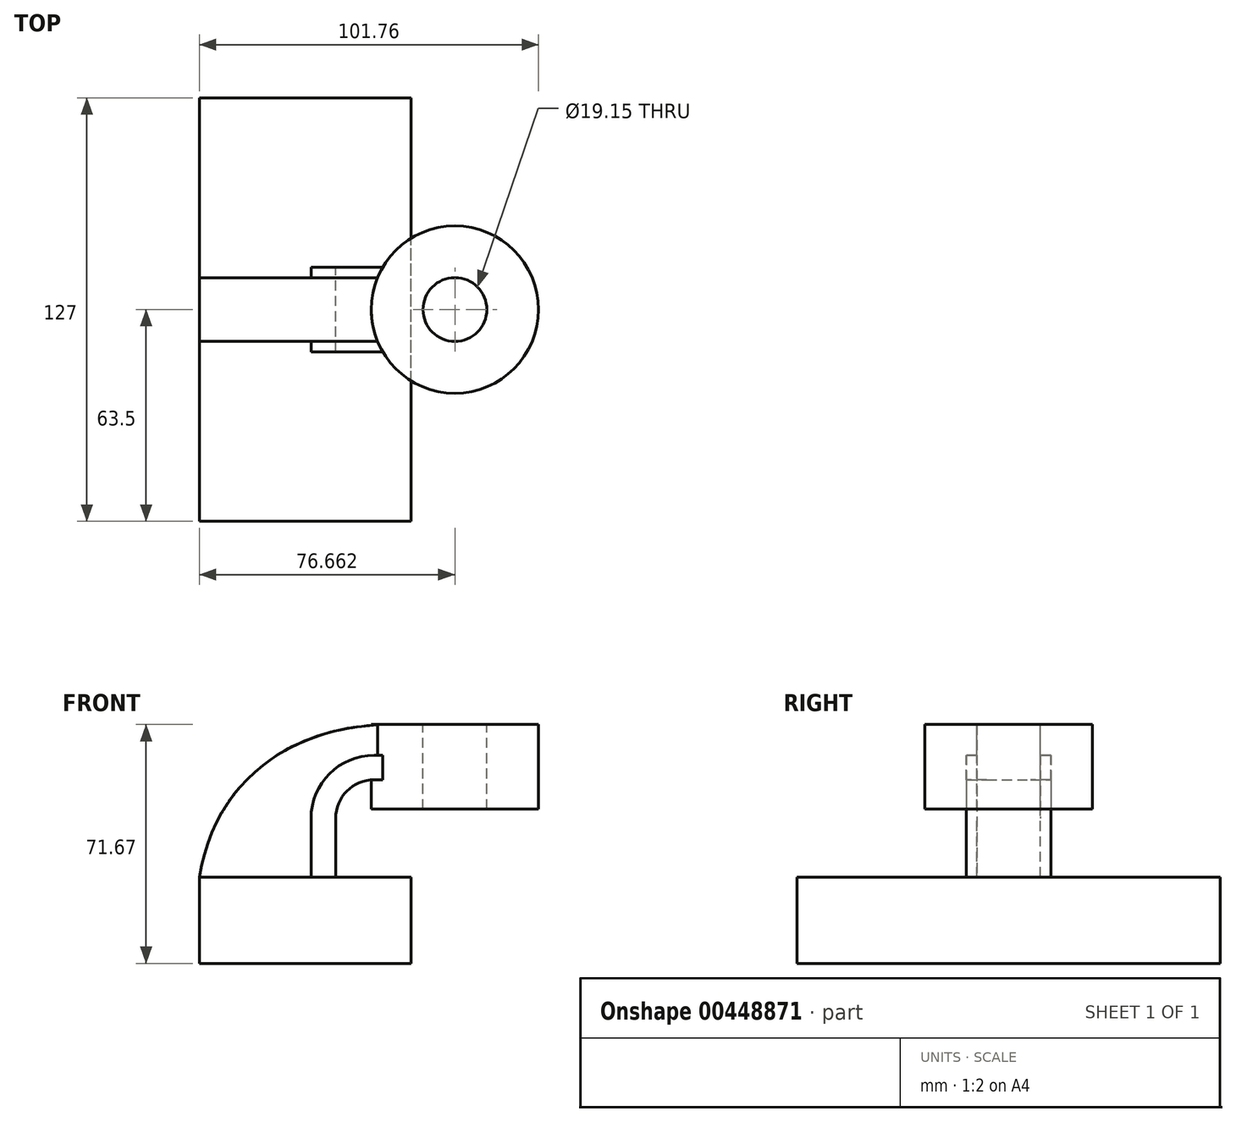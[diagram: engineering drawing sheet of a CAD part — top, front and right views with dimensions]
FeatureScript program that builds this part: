
annotation { "Feature Type Name" : "Feature", "Feature Type Description" : "" }
export const myFeature = defineFeature(function(context is Context, id is Id, definition is map)
    precondition{}
    {
        {
            var Q0;
            Q0=qCreatedBy(makeId("Front.planeOp"),FACE);
            var sketch = newSketch(context, id + "F0", { "sketchPlane" : qUnion([Q0])});
            skLineSegment(sketch, "E0.bottom", {"start": v(31.75, -12.95) * mm, "end": v(-31.75, -12.95) * mm});
            skLineSegment(sketch, "E0.top", {"start": v(31.75, 12.95) * mm, "end": v(-31.75, 12.95) * mm});
            skLineSegment(sketch, "E0.left", {"start": v(31.75, -12.95) * mm, "end": v(31.75, 12.95) * mm});
            skLineSegment(sketch, "E0.right", {"start": v(-31.75, -12.95) * mm, "end": v(-31.75, 12.95) * mm});
            skPoint(sketch, "E0.middle", {"position": v(0, 0) * mm});
            skLineSegment(sketch, "E1.bottom", {"start": v(64.65, 35.11) * mm, "end": v(25.17, 35.11) * mm});
            skLineSegment(sketch, "E1.top", {"start": v(64.65, 58.72) * mm, "end": v(25.17, 58.72) * mm});
            skLineSegment(sketch, "E1.left", {"start": v(64.65, 35.11) * mm, "end": v(64.65, 58.72) * mm});
            skLineSegment(sketch, "E1.right", {"start": v(25.17, 35.11) * mm, "end": v(25.17, 58.72) * mm});
            skPoint(sketch, "E1.middle", {"position": v(44.91, 46.92) * mm});
            skLineSegment(sketch, "E2", {"start": v(9.11, 12.95) * mm, "end": v(9.11, 30.56) * mm});
            skArc(sketch, "E3", {"start": v(9.11, 30.56) * mm, "mid": v(12.5, 38.74) * mm, "end": v(20.69, 42.14) * mm});
            skLineSegment(sketch, "E4", {"start": v(20.69, 42.14) * mm, "end": v(60.17, 42.14) * mm});
            skFitSpline(sketch, "E5", {"points": [v(-31.75, 12.95) * mm, v(25.17, 58.72) * mm], "startDerivative": vector(14.1, 86.06) * mm, "endDerivative": vector(90.2, 1.27) * mm});
            skLineSegment(sketch, "E6.0", {"start": v(20.69, 49.5) * mm, "end": v(60.17, 49.5) * mm});
            skArc(sketch, "E6.1", {"start": v(1.74, 30.56) * mm, "mid": v(7.3, 43.95) * mm, "end": v(20.69, 49.5) * mm});
            skLineSegment(sketch, "E6.2", {"start": v(1.74, 12.95) * mm, "end": v(1.74, 30.56) * mm});
            skLineSegment(sketch, "E7", {"start": v(44.91, 58.72) * mm, "end": v(44.91, 35.11) * mm});
            skSolve(sketch);
        }
        {
            var Q0;
            Q0=makeQuery(id+"F0.imprint","IMPRINT",FACE,{"disambiguationData":[TD([[makeQuery(id+"F0.imprint","IMPRINT",EDGE,{"derivedFrom":sQuery(id+"F0.wireOp",EDGE,"E0.bottom")}),-1.0]])]});
            extrude(context, id + "F1", {"entities" : qUnion([Q0]), "endBound" : BoundingType.SYMMETRIC, "depth" : 127 * mm});
        }
        {
            var Q0;
            {var subQ0=sQuery(id+"F0.wireOp",EDGE,"E5");Q0=makeQuery(id+"F0.imprint","IMPRINT",FACE,{"disambiguationData":[TD([[makeQuery(id+"F0.imprint","IMPRINT",EDGE,{"derivedFrom":subQ0}),-1.0]])]});}
            extrude(context, id + "F2", {"entities" : qUnion([Q0]), "operationType" : NewBodyOperationType.ADD, "endBound" : BoundingType.SYMMETRIC, "depth" : 19.05 * mm});
        }
        {
            var Q0;
            {var subQ1=sQuery(id+"F0.wireOp",EDGE,"E2");Q0=makeQuery(id+"F0.imprint","IMPRINT",FACE,{"disambiguationData":[TD([[makeQuery(id+"F0.imprint","IMPRINT",EDGE,{"derivedFrom":subQ1}),1.0]])]});}
            extrude(context, id + "F3", {"entities" : qUnion([Q0]), "operationType" : NewBodyOperationType.ADD, "endBound" : BoundingType.SYMMETRIC, "depth" : 25.4 * mm});
        }
        {
            var Q0;
            {var subQ0=sQuery(id+"F0.wireOp",EDGE,"E1.left");Q0=makeQuery(id+"F0.imprint","IMPRINT",FACE,{"disambiguationData":[TD([[makeQuery(id+"F0.imprint","IMPRINT",EDGE,{"derivedFrom":subQ0}),1.0]])]});}
            var Q1;
            Q1=sQuery(id+"F0.wireOp",EDGE,"E7");
            revolve(context, id + "F4", {"operationType" : NewBodyOperationType.ADD, "entities" : qUnion([Q0]), "axis" : qUnion([Q1]), "revolveType" : RevolveType.FULL});
        }
        {
            var Q0;
            Q0=makeQuery(id+"F4.opRevolve","SWEPT_FACE",FACE,{"disambiguationData":[OSD([sQuery(id+"F0.wireOp",EDGE,"E1.top")])]});
            var sketch = newSketch(context, id + "F5", { "sketchPlane" : qUnion([Q0])});
            skCircle(sketch, "E8", {"center": v(44.91, 0) * mm, "radius": 25.1 * mm});
            skSolve(sketch);
        }
        {
            var Q0;
            Q0 = qSketchRegion(id + "F5", true);
            extrude(context, id + "F6", {"entities" : qUnion([Q0]), "operationType" : NewBodyOperationType.ADD, "oppositeDirection" : true, "depth" : 25.4 * mm});
        }
        {
            var Q0;
            Q0=makeQuery(id+"F6.boolean.opBoolean","MERGE",FACE,{"derivedFrom":[makeQuery(id+"F4.opRevolve","SWEPT_FACE",FACE,{"disambiguationData":[OSD([sQuery(id+"F0.wireOp",EDGE,"E1.top")])]}),makeQuery(id+"F6.opExtrude","CAP_FACE",FACE,{"disambiguationData":[OSD([sQuery(id+"F5.wireOp",EDGE,"E8")])],"isStart":true})]});
            var sketch = newSketch(context, id + "F7", { "sketchPlane" : qUnion([Q0])});
            skCircle(sketch, "E9", {"center": v(44.91, 0) * mm, "radius": 8.64 * mm});
            skSolve(sketch);
        }
        {
            var Q0;
            Q0=sQuery(id+"F7.wireOp",VERTEX,"E9.center");
            var Q1;
            Q1=makeQuery(id+"F1.opExtrude","SWEPT_BODY",BODY,{"disambiguationData":[OSD([sQuery(id+"F0.wireOp",EDGE,"E0.bottom"),sQuery(id+"F0.wireOp",EDGE,"E0.top"),sQuery(id+"F0.wireOp",EDGE,"E0.left"),sQuery(id+"F0.wireOp",EDGE,"E0.right")])]});
            var Q2;
            Q2=makeQuery(id+"F4.opRevolve","SWEPT_BODY",BODY,{"disambiguationData":[OSD([sQuery(id+"F0.wireOp",EDGE,"E1.bottom"),sQuery(id+"F0.wireOp",EDGE,"E1.top"),sQuery(id+"F0.wireOp",EDGE,"E1.left"),sQuery(id+"F0.wireOp",EDGE,"E7")])]});
            hole(context, id + "F8", {"style" : HoleStyle.SIMPLE, "endStyle" : HoleEndStyle.THROUGH, "holeDiameter" : 19.15 * mm, "isTappedThrough" : true, "tappedDepth" : 12.7 * mm, "tapClearance" : 3, "locations" : qUnion([Q0]), "scope" : qUnion([Q1, Q2])});
        }
    });
